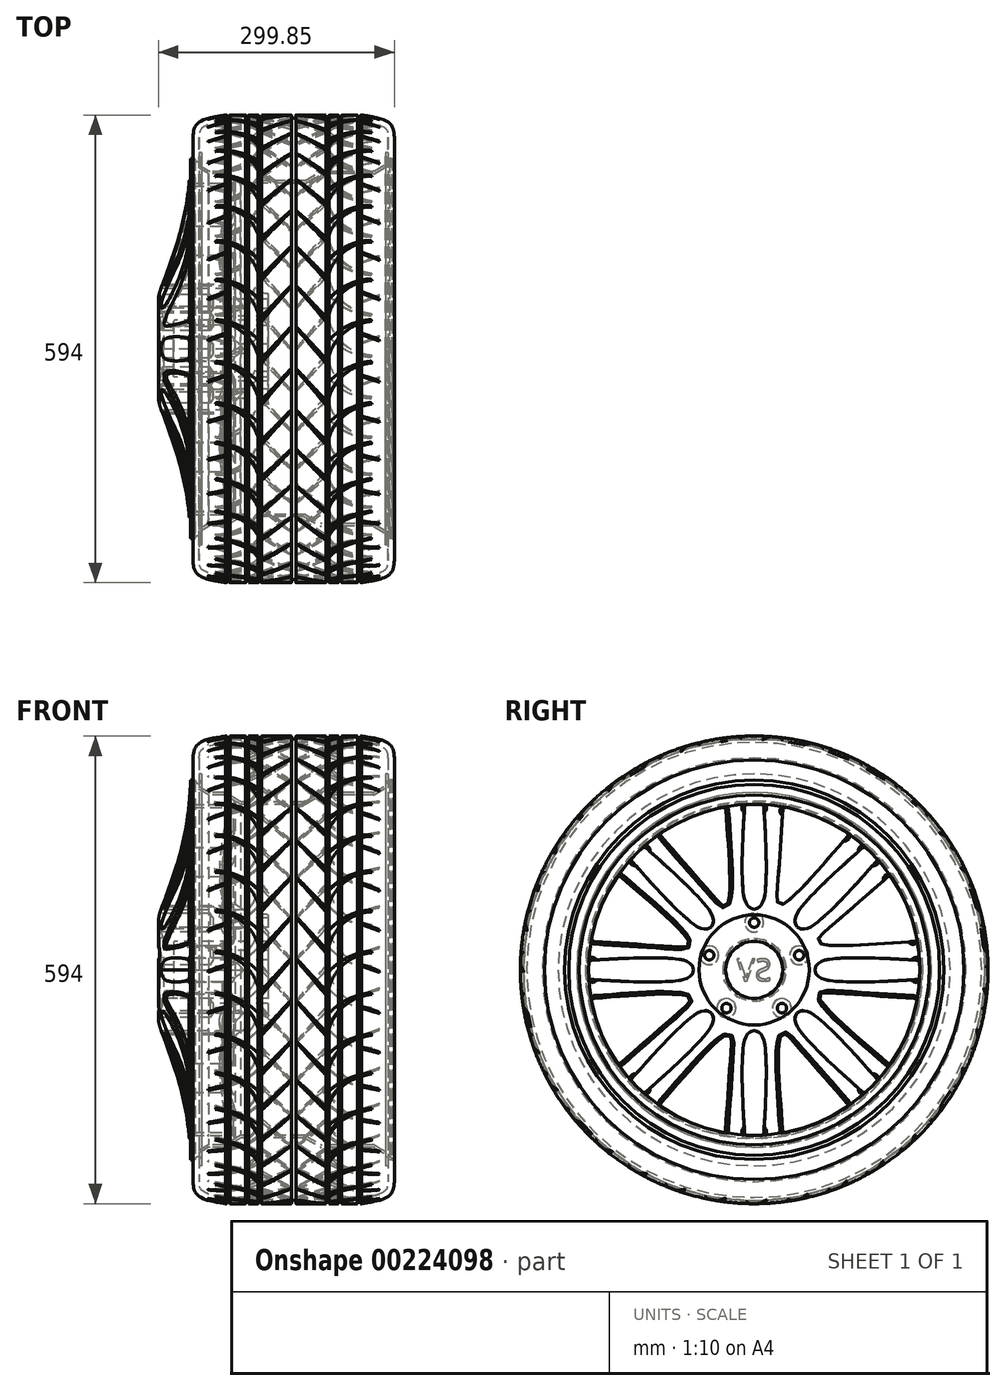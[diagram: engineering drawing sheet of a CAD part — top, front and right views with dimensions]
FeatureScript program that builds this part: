
annotation { "Feature Type Name" : "Feature", "Feature Type Description" : "" }
export const myFeature = defineFeature(function(context is Context, id is Id, definition is map)
    precondition{}
    {
        {
            var Q0;
            Q0=qCreatedBy(makeId("Front.planeOp"),FACE);
            var sketch = newSketch(context, id + "F0", { "sketchPlane" : qUnion([Q0])});
            skLineSegment(sketch, "E0", {"start": v(-128, 244.95) * mm, "end": v(-128, 266.43) * mm});
            skLineSegment(sketch, "E1", {"start": v(0, 297) * mm, "end": v(86.47, 297) * mm});
            skLineSegment(sketch, "E2", {"start": v(128, 266.43) * mm, "end": v(128, 244.95) * mm});
            skLineSegment(sketch, "E3", {"start": v(120, 249) * mm, "end": v(117, 249) * mm});
            skLineSegment(sketch, "E4", {"start": v(117, 249) * mm, "end": v(117, 241) * mm});
            skLineSegment(sketch, "E5", {"start": v(-120, 269) * mm, "end": v(-120, 249) * mm});
            skLineSegment(sketch, "E6", {"start": v(-120, 249) * mm, "end": v(-117, 249) * mm});
            skLineSegment(sketch, "E7", {"start": v(-117, 249) * mm, "end": v(-117, 241) * mm});
            skLineSegment(sketch, "E8", {"start": v(-128, 0) * mm, "end": v(128, 0) * mm});
            skArc(sketch, "E9", {"start": v(-125, 241) * mm, "mid": v(-121, 237) * mm, "end": v(-117, 241) * mm});
            skArc(sketch, "E10", {"start": v(117, 241) * mm, "mid": v(121, 237) * mm, "end": v(125, 241) * mm});
            skLineSegment(sketch, "E11", {"start": v(0, 297) * mm, "end": v(0, 289) * mm, "construction": true});
            skArc(sketch, "E12", {"start": v(-128, 244.95) * mm, "mid": v(-127.16, 242.47) * mm, "end": v(-125, 241) * mm});
            skArc(sketch, "E13", {"start": v(125, 241) * mm, "mid": v(127.16, 242.47) * mm, "end": v(128, 244.95) * mm});
            skFitSpline(sketch, "E14", {"points": [v(120, 269) * mm, v(117.14, 279.65) * mm, v(100, 286.7) * mm, v(86.47, 289) * mm], "startDerivative": vector(-1.21, 39.82) * mm, "endDerivative": vector(-44.37, 2.92) * mm});
            skFitSpline(sketch, "E15", {"points": [v(128, 266.43) * mm, v(124.6, 283.17) * mm, v(112.1, 291.85) * mm, v(98.12, 295.03) * mm, v(86.47, 297) * mm], "startDerivative": vector(-3.17, 67.96) * mm, "endDerivative": vector(-50.63, 8.67) * mm});
            skPoint(sketch, "E16.orphan", {"position": v(128, 297) * mm});
            skLineSegment(sketch, "E17.trimOffspring", {"start": v(120, 269) * mm, "end": v(120, 249) * mm});
            skFitSpline(sketch, "E18.MirrorCS", {"points": [v(-120, 269) * mm, v(-117.14, 279.65) * mm, v(-100, 286.7) * mm, v(-86.47, 289) * mm], "startDerivative": vector(1.21, 39.82) * mm, "endDerivative": vector(44.37, 2.92) * mm});
            skFitSpline(sketch, "E19.MirrorCS", {"points": [v(-128, 266.43) * mm, v(-124.6, 283.17) * mm, v(-112.1, 291.85) * mm, v(-98.12, 295.03) * mm, v(-86.47, 297) * mm], "startDerivative": vector(3.17, 67.96) * mm, "endDerivative": vector(50.63, 8.67) * mm});
            skPoint(sketch, "E20.orphan", {"position": v(-128, 297) * mm});
            skLineSegment(sketch, "E21.trimOffspring", {"start": v(-86.47, 289) * mm, "end": v(86.47, 289) * mm});
            skLineSegment(sketch, "E22", {"start": v(0, 297) * mm, "end": v(-86.47, 297) * mm});
            skSolve(sketch);
        }
        {
            var Q0;
            Q0=makeQuery(id+"F0.imprint","IMPRINT",FACE,{"disambiguationData":[TD([[makeQuery(id+"F0.imprint","IMPRINT",EDGE,{"derivedFrom":sQuery(id+"F0.wireOp",EDGE,"E0")}),-1.0]])]});
            var Q1;
            Q1=sQuery(id+"F0.wireOp",EDGE,"E8");
            revolve(context, id + "F1", {"entities" : qUnion([Q0]), "axis" : qUnion([Q1]), "revolveType" : RevolveType.FULL});
        }
        {
            var Q0;
            Q0=qCreatedBy(makeId("Front.planeOp"),FACE);
            var sketch = newSketch(context, id + "F2", { "sketchPlane" : qUnion([Q0])});
            skLineSegment(sketch, "E23.0", {"start": v(0, 297) * mm, "end": v(3, 297) * mm});
            skLineSegment(sketch, "E24.bottom", {"start": v(85, 297) * mm, "end": v(81, 297) * mm});
            skLineSegment(sketch, "E24.top", {"start": v(85, 293) * mm, "end": v(81, 293) * mm});
            skLineSegment(sketch, "E24.left", {"start": v(85, 297) * mm, "end": v(85, 293) * mm});
            skLineSegment(sketch, "E24.right", {"start": v(81, 297) * mm, "end": v(81, 293) * mm});
            skLineSegment(sketch, "E25.bottom", {"start": v(61, 297) * mm, "end": v(57, 297) * mm});
            skLineSegment(sketch, "E25.top", {"start": v(61, 293) * mm, "end": v(57, 293) * mm});
            skLineSegment(sketch, "E25.left", {"start": v(61, 297) * mm, "end": v(61, 293) * mm});
            skLineSegment(sketch, "E25.right", {"start": v(57, 297) * mm, "end": v(57, 293) * mm});
            skLineSegment(sketch, "E26.bottom", {"start": v(3, 297) * mm, "end": v(-3, 297) * mm});
            skLineSegment(sketch, "E26.top", {"start": v(3, 293) * mm, "end": v(-3, 293) * mm});
            skLineSegment(sketch, "E26.left", {"start": v(3, 297) * mm, "end": v(3, 293) * mm});
            skLineSegment(sketch, "E26.right", {"start": v(-3, 297) * mm, "end": v(-3, 293) * mm});
            skLineSegment(sketch, "E27.bottom", {"start": v(45, 297) * mm, "end": v(41, 297) * mm});
            skLineSegment(sketch, "E27.top", {"start": v(45, 293) * mm, "end": v(41, 293) * mm});
            skLineSegment(sketch, "E27.left", {"start": v(45, 297) * mm, "end": v(45, 293) * mm});
            skLineSegment(sketch, "E27.right", {"start": v(41, 297) * mm, "end": v(41, 293) * mm});
            skLineSegment(sketch, "E28.MirrorCS", {"start": v(-41, 297) * mm, "end": v(-41, 293) * mm});
            skLineSegment(sketch, "E29.MirrorCS", {"start": v(-45, 293) * mm, "end": v(-41, 293) * mm});
            skLineSegment(sketch, "E30.MirrorCS", {"start": v(-45, 297) * mm, "end": v(-45, 293) * mm});
            skLineSegment(sketch, "E31.MirrorCS", {"start": v(-57, 297) * mm, "end": v(-57, 293) * mm});
            skLineSegment(sketch, "E32.MirrorCS", {"start": v(-61, 293) * mm, "end": v(-57, 293) * mm});
            skLineSegment(sketch, "E33.MirrorCS", {"start": v(-61, 297) * mm, "end": v(-61, 293) * mm});
            skLineSegment(sketch, "E34.MirrorCS", {"start": v(-81, 297) * mm, "end": v(-81, 293) * mm});
            skLineSegment(sketch, "E35.MirrorCS", {"start": v(-85, 293) * mm, "end": v(-81, 293) * mm});
            skLineSegment(sketch, "E36.MirrorCS", {"start": v(-85, 297) * mm, "end": v(-85, 293) * mm});
            skLineSegment(sketch, "E37.MirrorCS", {"start": v(-45, 297) * mm, "end": v(-41, 297) * mm});
            skLineSegment(sketch, "E38.MirrorCS", {"start": v(-61, 297) * mm, "end": v(-57, 297) * mm});
            skLineSegment(sketch, "E39.MirrorCS", {"start": v(-85, 297) * mm, "end": v(-81, 297) * mm});
            skLineSegment(sketch, "E40.trimOffspring", {"start": v(41, 297) * mm, "end": v(45, 297) * mm});
            skLineSegment(sketch, "E41.trimOffspring", {"start": v(57, 297) * mm, "end": v(61, 297) * mm});
            skLineSegment(sketch, "E42.trimOffspring", {"start": v(81, 297) * mm, "end": v(85, 297) * mm});
            skPoint(sketch, "E43.orphan", {"position": v(86.47, 297) * mm});
            skSolve(sketch);
        }
        {
            var Q0;
            Q0=qSketchRegion(id+"F2",true);
            var Q1;
            Q1=sQuery(id+"F0.wireOp",EDGE,"E8");
            revolve(context, id + "F3", {"operationType" : NewBodyOperationType.REMOVE, "entities" : qUnion([Q0]), "axis" : qUnion([Q1]), "revolveType" : RevolveType.FULL, "oppositeDirection" : true});
        }
        {
            var Q0;
            Q0=sQuery(id+"F0.wireOp",VERTEX,"E22.start");
            var Q1;
            Q1=sQuery(id+"F0.wireOp",EDGE,"E11");
            cPlane(context, id + "F4", {"entities" : qUnion([Q0, Q1]), "cplaneType" : CPlaneType.CURVE_POINT, "offset" : 5 * mm, "width" : 150 * mm, "height" : 150 * mm});
        }
        {
            var Q0;
            Q0=qCreatedBy(id+"F4.planeOp",FACE);
            var sketch = newSketch(context, id + "F5", { "sketchPlane" : qUnion([Q0])});
            skPoint(sketch, "E44.0", {"position": v(0, 0) * mm});
            skLineSegment(sketch, "E45", {"start": v(-41, 12.66) * mm, "end": v(-3, -28.5) * mm});
            skLineSegment(sketch, "E46", {"start": v(-41, 18.65) * mm, "end": v(-3, -26.48) * mm});
            skLineSegment(sketch, "E47", {"start": v(0, 0) * mm, "end": v(0, 30) * mm, "construction": true});
            skLineSegment(sketch, "E48.MirrorCS", {"start": v(41, 12.66) * mm, "end": v(3, -28.5) * mm});
            skLineSegment(sketch, "E49.MirrorCS", {"start": v(41, 18.65) * mm, "end": v(3, -26.48) * mm});
            skLineSegment(sketch, "E50", {"start": v(-41, 18.65) * mm, "end": v(-41, 12.66) * mm});
            skLineSegment(sketch, "E51", {"start": v(-3, -28.5) * mm, "end": v(-3, -26.48) * mm});
            skLineSegment(sketch, "E52", {"start": v(3, -26.48) * mm, "end": v(3, -28.5) * mm});
            skLineSegment(sketch, "E53", {"start": v(41, 18.65) * mm, "end": v(41, 12.66) * mm});
            skArc(sketch, "E54", {"start": v(45, -11.11) * mm, "mid": v(74.04, -31.51) * mm, "end": v(109.1, -37) * mm});
            skArc(sketch, "E55", {"start": v(45, 8.9) * mm, "mid": v(69.14, -24.55) * mm, "end": v(109.1, -34.84) * mm});
            skLineSegment(sketch, "E56", {"start": v(109.1, -37) * mm, "end": v(109.1, -34.84) * mm});
            skLineSegment(sketch, "E57", {"start": v(45, -11.11) * mm, "end": v(45, 8.9) * mm});
            skLineSegment(sketch, "E58.MirrorCS", {"start": v(-109.1, -37) * mm, "end": v(-109.1, -34.84) * mm});
            skArc(sketch, "E59.MirrorCS", {"start": v(-45, -11.11) * mm, "mid": v(-74.04, -31.51) * mm, "end": v(-109.1, -37) * mm});
            skLineSegment(sketch, "E60.MirrorCS", {"start": v(-45, -11.11) * mm, "end": v(-45, 8.9) * mm});
            skArc(sketch, "E61.MirrorCS", {"start": v(-45, 8.9) * mm, "mid": v(-69.14, -24.55) * mm, "end": v(-109.1, -34.84) * mm});
            skLineSegment(sketch, "E62", {"start": v(85, -18.42) * mm, "end": v(108.99, -9.9) * mm});
            skLineSegment(sketch, "E63", {"start": v(85, -20.44) * mm, "end": v(108.99, -11.92) * mm});
            skLineSegment(sketch, "E64", {"start": v(108.99, -11.92) * mm, "end": v(108.99, -9.9) * mm});
            skLineSegment(sketch, "E65", {"start": v(85, -20.44) * mm, "end": v(85, -18.42) * mm});
            skLineSegment(sketch, "E66.MirrorCS", {"start": v(-85, -20.44) * mm, "end": v(-85, -18.42) * mm});
            skLineSegment(sketch, "E67.MirrorCS", {"start": v(-108.99, -11.92) * mm, "end": v(-108.99, -9.9) * mm});
            skLineSegment(sketch, "E68.MirrorCS", {"start": v(-85, -20.44) * mm, "end": v(-108.99, -11.92) * mm});
            skLineSegment(sketch, "E69.MirrorCS", {"start": v(-85, -18.42) * mm, "end": v(-108.99, -9.9) * mm});
            skSolve(sketch);
        }
        {
            var Q0;
            Q0=qSketchRegion(id+"F5",true);
            extrude(context, id + "F6", {"entities" : qUnion([Q0]), "depth" : 4.3 * mm});
        }
        {
            var Q0;
            Q0=makeQuery(id+"F6.opExtrude","SWEPT_BODY",BODY,{"disambiguationData":[OSD([sQuery(id+"F5.wireOp",EDGE,"E45"),sQuery(id+"F5.wireOp",EDGE,"E46"),sQuery(id+"F5.wireOp",EDGE,"E50"),sQuery(id+"F5.wireOp",EDGE,"E51")])]});
            var Q1;
            Q1=makeQuery(id+"F6.opExtrude","SWEPT_BODY",BODY,{"disambiguationData":[OSD([sQuery(id+"F5.wireOp",EDGE,"E48.MirrorCS"),sQuery(id+"F5.wireOp",EDGE,"E49.MirrorCS"),sQuery(id+"F5.wireOp",EDGE,"E52"),sQuery(id+"F5.wireOp",EDGE,"E53")])]});
            var Q2;
            Q2=makeQuery(id+"F6.opExtrude","SWEPT_BODY",BODY,{"disambiguationData":[OSD([sQuery(id+"F5.wireOp",EDGE,"E54"),sQuery(id+"F5.wireOp",EDGE,"E55"),sQuery(id+"F5.wireOp",EDGE,"E56"),sQuery(id+"F5.wireOp",EDGE,"E57")])]});
            var Q3;
            Q3=makeQuery(id+"F6.opExtrude","SWEPT_BODY",BODY,{"disambiguationData":[OSD([sQuery(id+"F5.wireOp",EDGE,"E58.MirrorCS"),sQuery(id+"F5.wireOp",EDGE,"E59.MirrorCS"),sQuery(id+"F5.wireOp",EDGE,"E60.MirrorCS"),sQuery(id+"F5.wireOp",EDGE,"E61.MirrorCS")])]});
            var Q4;
            Q4=makeQuery(id+"F6.opExtrude","SWEPT_BODY",BODY,{"disambiguationData":[OSD([sQuery(id+"F5.wireOp",EDGE,"E62"),sQuery(id+"F5.wireOp",EDGE,"E63"),sQuery(id+"F5.wireOp",EDGE,"E64"),sQuery(id+"F5.wireOp",EDGE,"E65")])]});
            var Q5;
            Q5=makeQuery(id+"F6.opExtrude","SWEPT_BODY",BODY,{"disambiguationData":[OSD([sQuery(id+"F5.wireOp",EDGE,"E66.MirrorCS"),sQuery(id+"F5.wireOp",EDGE,"E67.MirrorCS"),sQuery(id+"F5.wireOp",EDGE,"E68.MirrorCS"),sQuery(id+"F5.wireOp",EDGE,"E69.MirrorCS")])]});
            var Q6;
            Q6=sQuery(id+"F0.wireOp",EDGE,"E8");
            circularPattern(context, id + "F7", {"operationType" : NewBodyOperationType.REMOVE, "entities" : qUnion([Q0, Q1, Q2, Q3, Q4, Q5]), "axis" : qUnion([Q6]), "angle" : 360 * degree, "instanceCount" : round(35), "equalSpace" : true});
        }
        {
            var Q0;
            Q0=qCreatedBy(makeId("Front.planeOp"),FACE);
            var sketch = newSketch(context, id + "F8", { "sketchPlane" : qUnion([Q0])});
            skLineSegment(sketch, "E70", {"start": v(-170.5, 0) * mm, "end": v(125, 0) * mm});
            skLineSegment(sketch, "E71", {"start": v(-152.5, 0) * mm, "end": v(-152.5, 36.25) * mm});
            skLineSegment(sketch, "E72", {"start": v(-152.5, 36.25) * mm, "end": v(-32.5, 36.25) * mm});
            skLineSegment(sketch, "E73", {"start": v(-32.5, 36.25) * mm, "end": v(-32.5, 70) * mm});
            skLineSegment(sketch, "E74", {"start": v(102.02, 222.3) * mm, "end": v(125, 235.57) * mm});
            skLineSegment(sketch, "E75", {"start": v(125, 235.57) * mm, "end": v(125, 241.3) * mm});
            skLineSegment(sketch, "E76", {"start": v(125, 241.3) * mm, "end": v(122, 241.3) * mm});
            skLineSegment(sketch, "E77", {"start": v(102.02, 222.3) * mm, "end": v(35.16, 222.3) * mm});
            skLineSegment(sketch, "E78", {"start": v(35.16, 222.3) * mm, "end": v(14.37, 210.3) * mm});
            skLineSegment(sketch, "E79", {"start": v(14.37, 210.3) * mm, "end": v(-67.23, 210.3) * mm});
            skLineSegment(sketch, "E80", {"start": v(-67.23, 210.3) * mm, "end": v(-88.02, 222.3) * mm});
            skLineSegment(sketch, "E81", {"start": v(-88.02, 222.3) * mm, "end": v(-108.02, 222.3) * mm});
            skLineSegment(sketch, "E82", {"start": v(-108.02, 222.3) * mm, "end": v(-131, 235.57) * mm});
            skLineSegment(sketch, "E83", {"start": v(-131, 235.57) * mm, "end": v(-131, 241.3) * mm});
            skLineSegment(sketch, "E84", {"start": v(-131, 241.3) * mm, "end": v(-128, 241.3) * mm});
            skLineSegment(sketch, "E85.0", {"start": v(122, 237.3) * mm, "end": v(122, 241.3) * mm});
            skLineSegment(sketch, "E85.1", {"start": v(101.22, 225.3) * mm, "end": v(122, 237.3) * mm});
            skLineSegment(sketch, "E85.2", {"start": v(101.22, 225.3) * mm, "end": v(34.35, 225.3) * mm});
            skLineSegment(sketch, "E85.3", {"start": v(34.35, 225.3) * mm, "end": v(13.57, 213.3) * mm});
            skLineSegment(sketch, "E85.4", {"start": v(13.57, 213.3) * mm, "end": v(-66.43, 213.3) * mm});
            skLineSegment(sketch, "E85.5", {"start": v(-128, 237.3) * mm, "end": v(-128, 241.3) * mm});
            skLineSegment(sketch, "E85.6", {"start": v(-107.22, 225.3) * mm, "end": v(-128, 237.3) * mm});
            skLineSegment(sketch, "E85.7", {"start": v(-87.22, 225.3) * mm, "end": v(-107.22, 225.3) * mm});
            skLineSegment(sketch, "E85.8", {"start": v(-66.43, 213.3) * mm, "end": v(-87.22, 225.3) * mm});
            skLineSegment(sketch, "E86", {"start": v(-170.5, 0) * mm, "end": v(-170.5, 37.49) * mm});
            skFitSpline(sketch, "E87", {"points": [v(-165.54, 39.55) * mm, v(-168.06, 48.15) * mm, v(-171.62, 59.11) * mm, v(-169.25, 74.67) * mm, v(-148.34, 134.05) * mm, v(-134.39, 196.84) * mm, v(-131, 235.57) * mm], "startDerivative": vector(-23.26, 90.7) * mm, "endDerivative": vector(11.52, 191.45) * mm});
            skFitSpline(sketch, "E88", {"points": [v(-32.5, 70) * mm, v(-65.4, 77.45) * mm, v(-85.25, 101.16) * mm, v(-90.29, 133.45) * mm, v(-80.8, 197.46) * mm, v(-74.43, 214.45) * mm], "startDerivative": vector(-178.56, 14.97) * mm, "endDerivative": vector(43.2, 91.04) * mm});
            skArc(sketch, "E89", {"start": v(-165.54, 39.55) * mm, "mid": v(-168.7, 40.17) * mm, "end": v(-170.5, 37.49) * mm});
            skLineSegment(sketch, "E90", {"start": v(-107.22, 225.3) * mm, "end": v(-108.02, 255.3) * mm, "construction": true});
            skLineSegment(sketch, "E91", {"start": v(-108.02, 255.3) * mm, "end": v(101.22, 255.3) * mm, "construction": true});
            skLineSegment(sketch, "E92", {"start": v(101.22, 255.3) * mm, "end": v(101.22, 225.3) * mm, "construction": true});
            skPoint(sketch, "E93", {"position": v(-3.4, 255.3) * mm});
            skSolve(sketch);
        }
        {
            var Q0;
            {var subQ2=sQuery(id+"F8.wireOp",EDGE,"E71");Q0=makeQuery(id+"F8.imprint","IMPRINT",FACE,{"disambiguationData":[TD([[makeQuery(id+"F8.imprint","IMPRINT",EDGE,{"derivedFrom":subQ2}),1.0]])]});}
            var Q1;
            Q1=sQuery(id+"F8.wireOp",EDGE,"E70");
            revolve(context, id + "F9", {"entities" : qUnion([Q0]), "axis" : qUnion([Q1]), "revolveType" : RevolveType.FULL});
        }
        {
            var Q0;
            Q0=makeQuery(id+"F8.imprint","IMPRINT",FACE,{"disambiguationData":[TD([[makeQuery(id+"F8.imprint","IMPRINT",EDGE,{"derivedFrom":sQuery(id+"F8.wireOp",EDGE,"E74")}),1.0]])]});
            var Q1;
            Q1=sQuery(id+"F8.wireOp",EDGE,"E70");
            revolve(context, id + "F10", {"entities" : qUnion([Q0]), "axis" : qUnion([Q1]), "revolveType" : RevolveType.FULL});
        }
        {
            var Q0;
            Q0=makeQuery(id+"F9.opRevolve","SWEPT_FACE",FACE,{"disambiguationData":[OSD([sQuery(id+"F8.wireOp",EDGE,"E73")])]});
            var sketch = newSketch(context, id + "F11", { "sketchPlane" : qUnion([Q0])});
            skCircle(sketch, "E94", {"center": v(0, 60) * mm, "radius": 6 * mm});
            skPoint(sketch, "E95.0", {"position": v(0, 0) * mm});
            skCircle(sketch, "E96.1.0", {"center": v(-57.06, 18.54) * mm, "radius": 6 * mm});
            skCircle(sketch, "E96.2.0", {"center": v(-35.27, -48.54) * mm, "radius": 6 * mm});
            skCircle(sketch, "E97.0.3.0", {"center": v(35.27, -48.54) * mm, "radius": 6 * mm});
            skCircle(sketch, "E97.0.4.0", {"center": v(57.06, 18.54) * mm, "radius": 6 * mm});
            skPoint(sketch, "E98.0", {"position": v(0, 210.3) * mm});
            skArc(sketch, "E99", {"start": v(12.06, 209.95) * mm, "mid": v(0, 210.3) * mm, "end": v(-12.06, 209.95) * mm});
            skFitSpline(sketch, "E100", {"points": [v(-12.06, 209.95) * mm, v(-15.11, 148.8) * mm, v(-14.17, 100.77) * mm, v(-9.46, 83.19) * mm, v(0, 77) * mm], "startDerivative": vector(-11.14, -175.96) * mm, "endDerivative": vector(83.69, -7.97) * mm});
            skLineSegment(sketch, "E101", {"start": v(0, 60) * mm, "end": v(0, 77) * mm, "construction": true});
            skFitSpline(sketch, "E102", {"points": [v(36.64, 207.08) * mm, v(29.5, 101.83) * mm, v(32.97, 82.07) * mm, v(98.48, 146.54) * mm, v(120.7, 172.21) * mm], "startDerivative": vector(-23.36, -349.3) * mm, "endDerivative": vector(82.69, 95.15) * mm});
            skArc(sketch, "E103.trimOffspring", {"start": v(120.7, 172.21) * mm, "mid": v(80.58, 194.25) * mm, "end": v(36.64, 207.08) * mm});
            skFitSpline(sketch, "E104.MirrorCS", {"points": [v(12.06, 209.95) * mm, v(15.11, 148.8) * mm, v(14.17, 100.77) * mm, v(9.46, 83.19) * mm, v(0, 77) * mm], "startDerivative": vector(11.14, -175.96) * mm, "endDerivative": vector(-83.69, -7.97) * mm});
            skSolve(sketch);
        }
        {
            var Q0;
            Q0=makeQuery(id+"F11.imprint","IMPRINT",FACE,{"disambiguationData":[TD([[makeQuery(id+"F11.imprint","IMPRINT",EDGE,{"derivedFrom":sQuery(id+"F11.wireOp",EDGE,"E99")}),1.0]])]});
            var Q1;
            Q1=makeQuery(id+"F11.imprint","IMPRINT",FACE,{"disambiguationData":[TD([[makeQuery(id+"F11.imprint","IMPRINT",EDGE,{"derivedFrom":sQuery(id+"F11.wireOp",EDGE,"E102")}),1.0]])]});
            var Q2;
            Q2=makeQuery(id+"F9.opRevolve","SWEPT_BODY",BODY,{"disambiguationData":[OSD([sQuery(id+"F8.wireOp",EDGE,"E70"),sQuery(id+"F8.wireOp",EDGE,"E71"),sQuery(id+"F8.wireOp",EDGE,"E72"),sQuery(id+"F8.wireOp",EDGE,"E73"),sQuery(id+"F8.wireOp",EDGE,"E80"),sQuery(id+"F8.wireOp",EDGE,"E81"),sQuery(id+"F8.wireOp",EDGE,"E82"),sQuery(id+"F8.wireOp",EDGE,"E86"),sQuery(id+"F8.wireOp",EDGE,"E87"),sQuery(id+"F8.wireOp",EDGE,"E88"),sQuery(id+"F8.wireOp",EDGE,"E89")])]});
            extrude(context, id + "F12", {"entities" : qUnion([Q0, Q1]), "oppositeDirection" : true, "endBoundEntityBody" : qUnion([Q2]), "depth" : 150 * mm});
        }
        {
            var Q0;
            Q0=makeQuery(id+"F12.opExtrude","SWEPT_BODY",BODY,{"disambiguationData":[OSD([sQuery(id+"F11.wireOp",EDGE,"E99"),sQuery(id+"F11.wireOp",EDGE,"E100"),sQuery(id+"F11.wireOp",EDGE,"E104.MirrorCS")])]});
            var Q1;
            Q1=makeQuery(id+"F12.opExtrude","SWEPT_BODY",BODY,{"disambiguationData":[OSD([sQuery(id+"F11.wireOp",EDGE,"E102"),sQuery(id+"F11.wireOp",EDGE,"E103.trimOffspring")])]});
            var Q2;
            Q2=sQuery(id+"F8.wireOp",EDGE,"E70");
            circularPattern(context, id + "F13", {"operationType" : NewBodyOperationType.REMOVE, "entities" : qUnion([Q0, Q1]), "axis" : qUnion([Q2]), "angle" : 360 * degree, "instanceCount" : round(8), "equalSpace" : true});
        }
        {
            var Q0;
            Q0=makeQuery(id+"F11.imprint","IMPRINT",FACE,{"disambiguationData":[TD([[makeQuery(id+"F11.imprint","IMPRINT",EDGE,{"derivedFrom":sQuery(id+"F11.wireOp",EDGE,"E94")}),-1.0]])]});
            cPlane(context, id + "F14", {"entities" : qUnion([Q0]), "cplaneType" : CPlaneType.OFFSET, "offset" : 150 * mm, "oppositeDirection" : true, "width" : 150 * mm, "height" : 150 * mm});
        }
        {
            var Q0;
            Q0=qCreatedBy(id+"F14.planeOp",FACE);
            var sketch = newSketch(context, id + "F15", { "sketchPlane" : qUnion([Q0])});
            skPoint(sketch, "E105.0", {"position": v(-35.27, -48.54) * mm});
            skPoint(sketch, "E105.1", {"position": v(-57.06, 18.54) * mm});
            skPoint(sketch, "E105.2", {"position": v(0, 60) * mm});
            skPoint(sketch, "E105.3", {"position": v(57.06, 18.54) * mm});
            skPoint(sketch, "E105.4", {"position": v(35.27, -48.54) * mm});
            skSolve(sketch);
        }
        {
            var Q0;
            Q0=sQuery(id+"F15.wireOp",VERTEX,"E105.3");
            var Q1;
            Q1=sQuery(id+"F15.wireOp",VERTEX,"E105.4");
            var Q2;
            Q2=sQuery(id+"F15.wireOp",VERTEX,"E105.0");
            var Q3;
            Q3=sQuery(id+"F15.wireOp",VERTEX,"E105.1");
            var Q4;
            Q4=sQuery(id+"F15.wireOp",VERTEX,"E105.2");
            var Q5;
            Q5=makeQuery(id+"F9.opRevolve","SWEPT_BODY",BODY,{"disambiguationData":[OSD([sQuery(id+"F8.wireOp",EDGE,"E70"),sQuery(id+"F8.wireOp",EDGE,"E71"),sQuery(id+"F8.wireOp",EDGE,"E72"),sQuery(id+"F8.wireOp",EDGE,"E73"),sQuery(id+"F8.wireOp",EDGE,"E80"),sQuery(id+"F8.wireOp",EDGE,"E81"),sQuery(id+"F8.wireOp",EDGE,"E82"),sQuery(id+"F8.wireOp",EDGE,"E86"),sQuery(id+"F8.wireOp",EDGE,"E87"),sQuery(id+"F8.wireOp",EDGE,"E88"),sQuery(id+"F8.wireOp",EDGE,"E89")])]});
            hole(context, id + "F16", {"style" : HoleStyle.SIMPLE, "holeDiameter" : 24 * mm, "endStyle" : HoleEndStyle.BLIND, "oppositeDirection" : true, "holeDepth" : 62 * mm, "locations" : qUnion([Q0, Q1, Q2, Q3, Q4]), "scope" : qUnion([Q5])});
        }
        {
            var Q0;
            Q0=sQuery(id+"F15.wireOp",VERTEX,"E105.4");
            var Q1;
            Q1=sQuery(id+"F15.wireOp",VERTEX,"E105.0");
            var Q2;
            Q2=sQuery(id+"F15.wireOp",VERTEX,"E105.1");
            var Q3;
            Q3=sQuery(id+"F15.wireOp",VERTEX,"E105.3");
            var Q4;
            Q4=sQuery(id+"F15.wireOp",VERTEX,"E105.2");
            var Q5;
            Q5=makeQuery(id+"F9.opRevolve","SWEPT_BODY",BODY,{"disambiguationData":[OSD([sQuery(id+"F8.wireOp",EDGE,"E70"),sQuery(id+"F8.wireOp",EDGE,"E71"),sQuery(id+"F8.wireOp",EDGE,"E72"),sQuery(id+"F8.wireOp",EDGE,"E73"),sQuery(id+"F8.wireOp",EDGE,"E80"),sQuery(id+"F8.wireOp",EDGE,"E81"),sQuery(id+"F8.wireOp",EDGE,"E82"),sQuery(id+"F8.wireOp",EDGE,"E86"),sQuery(id+"F8.wireOp",EDGE,"E87"),sQuery(id+"F8.wireOp",EDGE,"E88"),sQuery(id+"F8.wireOp",EDGE,"E89")])]});
            hole(context, id + "F17", {"style" : HoleStyle.C_SINK, "holeDiameter" : 12 * mm, "cSinkDiameter" : 24 * mm, "endStyle" : HoleEndStyle.THROUGH, "oppositeDirection" : true, "locations" : qUnion([Q0, Q1, Q2, Q3, Q4]), "scope" : qUnion([Q5]), "cSinkAngle" : 90 * degree});
        }
        {
            var Q0;
            Q0=makeQuery(id+"F13.boolean.opBoolean","COPY",FACE,{"derivedFrom":makeQuery(id+"F13.opPattern","COPY",FACE,{"derivedFrom":makeQuery(id+"F12.opExtrude","SWEPT_FACE",FACE,{"disambiguationData":[OSD([sQuery(id+"F11.wireOp",EDGE,"E102")])]}),"instanceName":"1"})});
            var Q1;
            Q1=makeQuery(id+"F13.boolean.opBoolean","COPY",FACE,{"derivedFrom":makeQuery(id+"F13.opPattern","COPY",FACE,{"derivedFrom":makeQuery(id+"F12.opExtrude","SWEPT_FACE",FACE,{"disambiguationData":[OSD([sQuery(id+"F11.wireOp",EDGE,"E102")])]}),"instanceName":"2"})});
            var Q2;
            Q2=makeQuery(id+"F13.boolean.opBoolean","COPY",FACE,{"derivedFrom":makeQuery(id+"F13.opPattern","COPY",FACE,{"derivedFrom":makeQuery(id+"F12.opExtrude","SWEPT_FACE",FACE,{"disambiguationData":[OSD([sQuery(id+"F11.wireOp",EDGE,"E102")])]}),"instanceName":"4"})});
            var Q3;
            Q3=makeQuery(id+"F13.boolean.opBoolean","COPY",FACE,{"derivedFrom":makeQuery(id+"F13.opPattern","COPY",FACE,{"derivedFrom":makeQuery(id+"F12.opExtrude","SWEPT_FACE",FACE,{"disambiguationData":[OSD([sQuery(id+"F11.wireOp",EDGE,"E102")])]}),"instanceName":"5"})});
            var Q4;
            Q4=makeQuery(id+"F13.boolean.opBoolean","COPY",FACE,{"derivedFrom":makeQuery(id+"F13.opPattern","COPY",FACE,{"derivedFrom":makeQuery(id+"F12.opExtrude","SWEPT_FACE",FACE,{"disambiguationData":[OSD([sQuery(id+"F11.wireOp",EDGE,"E102")])]}),"instanceName":"6"})});
            var Q5;
            Q5=makeQuery(id+"F13.boolean.opBoolean","COPY",FACE,{"derivedFrom":makeQuery(id+"F13.opPattern","COPY",FACE,{"derivedFrom":makeQuery(id+"F12.opExtrude","SWEPT_FACE",FACE,{"disambiguationData":[OSD([sQuery(id+"F11.wireOp",EDGE,"E103.trimOffspring")])]}),"instanceName":"7"})});
            var Q6;
            Q6=makeQuery(id+"F13.boolean.opBoolean","COPY",FACE,{"derivedFrom":makeQuery(id+"F13.opPattern","COPY",FACE,{"derivedFrom":makeQuery(id+"F12.opExtrude","SWEPT_FACE",FACE,{"disambiguationData":[OSD([sQuery(id+"F11.wireOp",EDGE,"E99")])]}),"instanceName":"7"})});
            var Q7;
            Q7=makeQuery(id+"F13.boolean.opBoolean","COPY",FACE,{"derivedFrom":makeQuery(id+"F12.opExtrude","SWEPT_FACE",FACE,{"disambiguationData":[OSD([sQuery(id+"F11.wireOp",EDGE,"E103.trimOffspring")])]})});
            var Q8;
            Q8=makeQuery(id+"F13.boolean.opBoolean","COPY",FACE,{"derivedFrom":makeQuery(id+"F12.opExtrude","SWEPT_FACE",FACE,{"disambiguationData":[OSD([sQuery(id+"F11.wireOp",EDGE,"E99")])]})});
            var Q9;
            Q9=makeQuery(id+"F13.boolean.opBoolean","COPY",FACE,{"derivedFrom":makeQuery(id+"F13.opPattern","COPY",FACE,{"derivedFrom":makeQuery(id+"F12.opExtrude","SWEPT_FACE",FACE,{"disambiguationData":[OSD([sQuery(id+"F11.wireOp",EDGE,"E99")])]}),"instanceName":"6"})});
            var Q10;
            Q10=makeQuery(id+"F13.boolean.opBoolean","COPY",FACE,{"derivedFrom":makeQuery(id+"F13.opPattern","COPY",FACE,{"derivedFrom":makeQuery(id+"F12.opExtrude","SWEPT_FACE",FACE,{"disambiguationData":[OSD([sQuery(id+"F11.wireOp",EDGE,"E99")])]}),"instanceName":"5"})});
            var Q11;
            Q11=makeQuery(id+"F13.boolean.opBoolean","COPY",FACE,{"derivedFrom":makeQuery(id+"F13.opPattern","COPY",FACE,{"derivedFrom":makeQuery(id+"F12.opExtrude","SWEPT_FACE",FACE,{"disambiguationData":[OSD([sQuery(id+"F11.wireOp",EDGE,"E99")])]}),"instanceName":"4"})});
            var Q12;
            Q12=makeQuery(id+"F13.boolean.opBoolean","COPY",FACE,{"derivedFrom":makeQuery(id+"F13.opPattern","COPY",FACE,{"derivedFrom":makeQuery(id+"F12.opExtrude","SWEPT_FACE",FACE,{"disambiguationData":[OSD([sQuery(id+"F11.wireOp",EDGE,"E99")])]}),"instanceName":"3"})});
            var Q13;
            Q13=makeQuery(id+"F13.boolean.opBoolean","COPY",FACE,{"derivedFrom":makeQuery(id+"F13.opPattern","COPY",FACE,{"derivedFrom":makeQuery(id+"F12.opExtrude","SWEPT_FACE",FACE,{"disambiguationData":[OSD([sQuery(id+"F11.wireOp",EDGE,"E99")])]}),"instanceName":"2"})});
            var Q14;
            Q14=makeQuery(id+"F13.boolean.opBoolean","COPY",FACE,{"derivedFrom":makeQuery(id+"F13.opPattern","COPY",FACE,{"derivedFrom":makeQuery(id+"F12.opExtrude","SWEPT_FACE",FACE,{"disambiguationData":[OSD([sQuery(id+"F11.wireOp",EDGE,"E99")])]}),"instanceName":"1"})});
            var Q15;
            Q15=makeQuery(id+"F13.boolean.opBoolean","COPY",FACE,{"derivedFrom":makeQuery(id+"F13.opPattern","COPY",FACE,{"derivedFrom":makeQuery(id+"F12.opExtrude","SWEPT_FACE",FACE,{"disambiguationData":[OSD([sQuery(id+"F11.wireOp",EDGE,"E102")])]}),"instanceName":"3"})});
            fillet(context, id + "F18", {"entities" : qUnion([Q0, Q1, Q2, Q3, Q4, Q5, Q6, Q7, Q8, Q9, Q10, Q11, Q12, Q13, Q14, Q15]), "radius" : 3.5 * mm, "tangentPropagation" : true, "allowEdgeOverflow" : false});
        }
        {
            var Q0;
            Q0=makeQuery(id+"F9.opRevolve","SWEPT_FACE",FACE,{"disambiguationData":[OSD([sQuery(id+"F8.wireOp",EDGE,"E86")])]});
            var sketch = newSketch(context, id + "F19", { "sketchPlane" : qUnion([Q0])});
            skText(sketch, "E106", { "text": "SV", "fontName": "OpenSans-Regular.ttf"});
            const initialGuessF19  = {"E106": [-0.0222, -0.01397, 1, 0, 0.02794]};
            skSetInitialGuess(sketch, initialGuessF19);
            skSolve(sketch);
        }
        {
            var Q0;
            Q0=qSketchRegion(id+"F19",true);
            extrude(context, id + "F20", {"entities" : qUnion([Q0]), "operationType" : NewBodyOperationType.ADD, "depth" : 1 * mm});
        }
        {
            var Q0;
            Q0=makeQuery(id+"F10.opRevolve","SWEPT_EDGE",EDGE,{"disambiguationData":[OSD([sQuery(id+"F8.wireOp",EDGE,"E85.4"),sQuery(id+"F8.wireOp",EDGE,"E85.8")])]});
            var Q1;
            Q1=makeQuery(id+"F10.opRevolve","SWEPT_EDGE",EDGE,{"disambiguationData":[OSD([sQuery(id+"F8.wireOp",EDGE,"E85.3"),sQuery(id+"F8.wireOp",EDGE,"E85.4")])]});
            var Q2;
            Q2=makeQuery(id+"F10.opRevolve","SWEPT_EDGE",EDGE,{"disambiguationData":[OSD([sQuery(id+"F8.wireOp",EDGE,"E85.2"),sQuery(id+"F8.wireOp",EDGE,"E85.3")])]});
            var Q3;
            Q3=makeQuery(id+"F10.opRevolve","SWEPT_EDGE",EDGE,{"disambiguationData":[OSD([sQuery(id+"F8.wireOp",EDGE,"E85.1"),sQuery(id+"F8.wireOp",EDGE,"E85.2")])]});
            var Q4;
            Q4=makeQuery(id+"F10.opRevolve","SWEPT_EDGE",EDGE,{"disambiguationData":[OSD([sQuery(id+"F8.wireOp",EDGE,"E85.7"),sQuery(id+"F8.wireOp",EDGE,"E85.8")])]});
            var Q5;
            Q5=makeQuery(id+"F10.opRevolve","SWEPT_EDGE",EDGE,{"disambiguationData":[OSD([sQuery(id+"F8.wireOp",EDGE,"E85.6"),sQuery(id+"F8.wireOp",EDGE,"E85.7")])]});
            var Q6;
            Q6=makeQuery(id+"F10.opRevolve","SWEPT_EDGE",EDGE,{"disambiguationData":[OSD([sQuery(id+"F8.wireOp",EDGE,"E85.0"),sQuery(id+"F8.wireOp",EDGE,"E85.1")])]});
            var Q7;
            Q7=makeQuery(id+"F10.opRevolve","SWEPT_EDGE",EDGE,{"disambiguationData":[OSD([sQuery(id+"F8.wireOp",EDGE,"E85.5"),sQuery(id+"F8.wireOp",EDGE,"E85.6")])]});
            fillet(context, id + "F21", {"entities" : qUnion([Q0, Q1, Q2, Q3, Q4, Q5, Q6, Q7]), "radius" : 3 * mm, "tangentPropagation" : true, "allowEdgeOverflow" : false});
        }
        {
            var Q0;
            Q0=makeQuery(id+"F10.opRevolve","SWEPT_EDGE",EDGE,{"disambiguationData":[OSD([sQuery(id+"F8.wireOp",EDGE,"E74"),sQuery(id+"F8.wireOp",EDGE,"E77")])]});
            var Q1;
            Q1=makeQuery(id+"F10.opRevolve","SWEPT_EDGE",EDGE,{"disambiguationData":[OSD([sQuery(id+"F8.wireOp",EDGE,"E77"),sQuery(id+"F8.wireOp",EDGE,"E78")])]});
            var Q2;
            Q2=makeQuery(id+"F10.opRevolve","SWEPT_EDGE",EDGE,{"disambiguationData":[OSD([sQuery(id+"F8.wireOp",EDGE,"E78"),sQuery(id+"F8.wireOp",EDGE,"E79")])]});
            fillet(context, id + "F22", {"entities" : qUnion([Q0, Q1, Q2]), "radius" : 3 * mm, "tangentPropagation" : true, "allowEdgeOverflow" : false});
        }
        {
            var Q0;
            Q0=makeQuery(id+"F9.opRevolve","SWEPT_EDGE",EDGE,{"disambiguationData":[OSD([sQuery(id+"F8.wireOp",EDGE,"E71"),sQuery(id+"F8.wireOp",EDGE,"E72")])]});
            fillet(context, id + "F23", {"entities" : qUnion([Q0]), "radius" : 2 * mm, "tangentPropagation" : true, "allowEdgeOverflow" : false});
        }
    });
